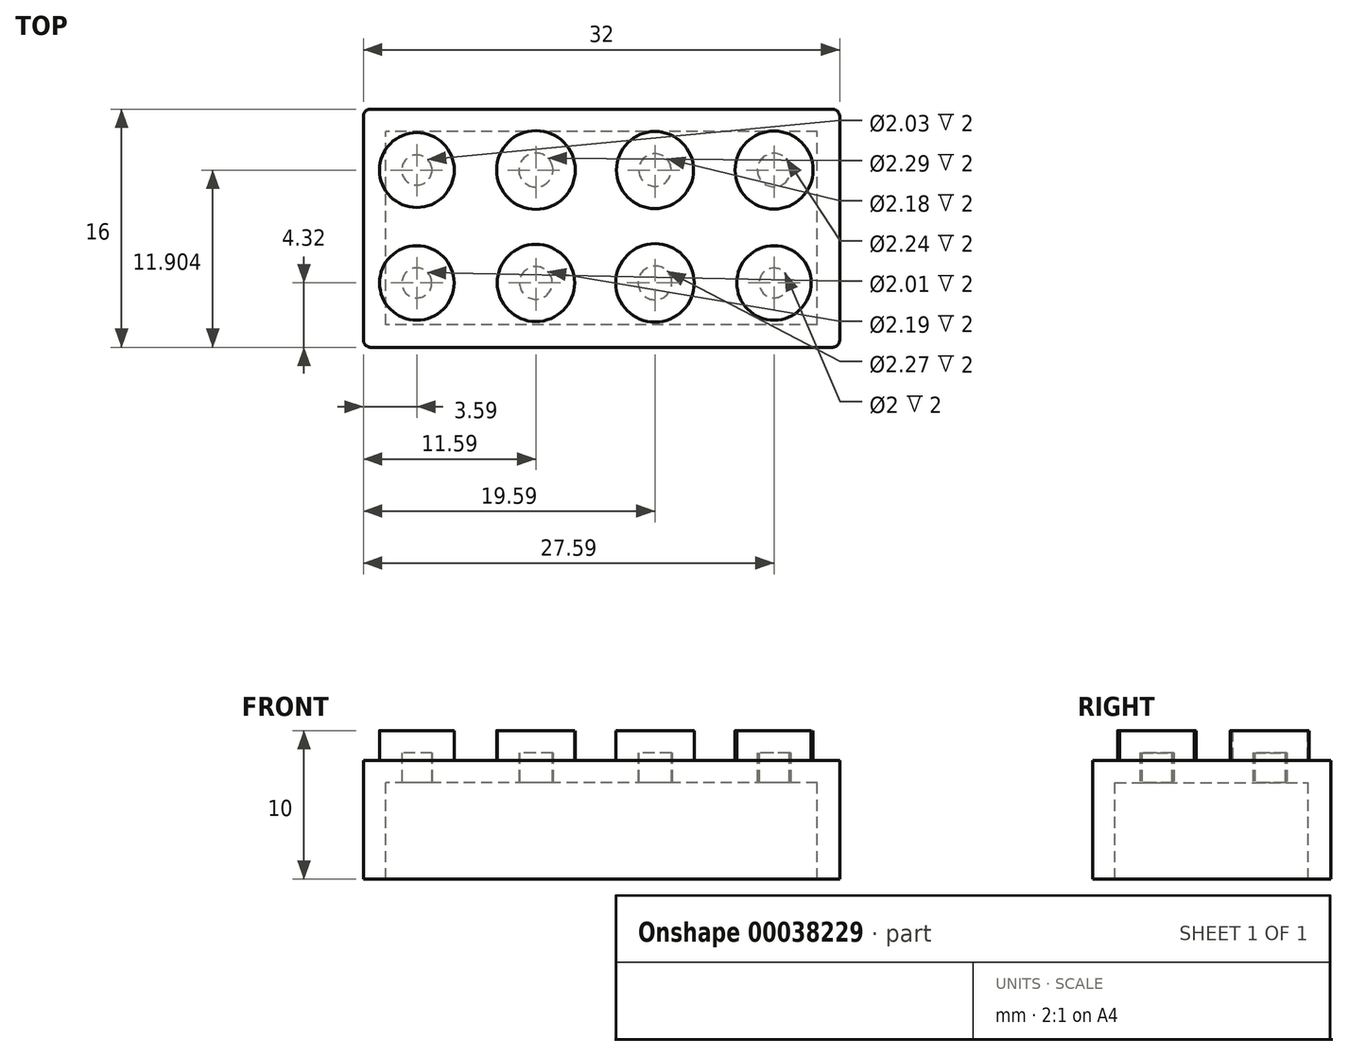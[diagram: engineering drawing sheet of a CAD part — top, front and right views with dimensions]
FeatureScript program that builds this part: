
annotation { "Feature Type Name" : "Feature", "Feature Type Description" : "" }
export const myFeature = defineFeature(function(context is Context, id is Id, definition is map)
    precondition{}
    {
        {
            var Q0;
            Q0=qCreatedBy(makeId("Top.planeOp"),FACE);
            var sketch = newSketch(context, id + "F0", { "sketchPlane" : qUnion([Q0])});
            skLineSegment(sketch, "E0.rect.bottom", {"start": v(16, -6.37) * mm, "end": v(-16, -6.37) * mm});
            skLineSegment(sketch, "E0.rect.top", {"start": v(16, 9.63) * mm, "end": v(-16, 9.63) * mm});
            skLineSegment(sketch, "E0.rect.left", {"start": v(16, -6.37) * mm, "end": v(16, 9.63) * mm});
            skLineSegment(sketch, "E0.rect.right", {"start": v(-16, -6.37) * mm, "end": v(-16, 9.63) * mm});
            skPoint(sketch, "E0.rect.middle", {"position": v(0, 1.63) * mm});
            skSolve(sketch);
        }
        {
            var Q0;
            Q0 = qSketchRegion(id + "F0", true);
            extrude(context, id + "F1", {"entities" : qUnion([Q0]), "depth" : 8 * mm});
        }
        {
            var Q0;
            Q0=qCreatedBy(makeId("Top.planeOp"),FACE);
            var Q1;
            Q1 = qBodyType(qCreatedBy(id + "F3" ,EDGE), BodyType.WIRE);
            cPlane(context, id + "F2", {"entities" : qUnion([Q0, Q1]), "cplaneType" : CPlaneType.OFFSET, "offset" : 8 * mm, "width" : 150 * mm, "height" : 150 * mm});
        }
        {
            var Q0;
            Q0=qCreatedBy(id+"F2.planeOp",FACE);
            var sketch = newSketch(context, id + "F3", { "sketchPlane" : qUnion([Q0])});
            skCircle(sketch, "E1", {"center": v(-12.41, 5.53) * mm, "radius": 2.51 * mm});
            skCircle(sketch, "E2", {"center": v(-4.41, 5.53) * mm, "radius": 2.64 * mm});
            skCircle(sketch, "E3", {"center": v(3.59, 5.53) * mm, "radius": 2.59 * mm});
            skCircle(sketch, "E4", {"center": v(11.59, 5.53) * mm, "radius": 2.62 * mm});
            skCircle(sketch, "E5", {"center": v(-12.41, -2.05) * mm, "radius": 2.5 * mm});
            skCircle(sketch, "E6", {"center": v(-4.41, -2.05) * mm, "radius": 2.6 * mm});
            skCircle(sketch, "E7", {"center": v(3.59, -2.05) * mm, "radius": 2.64 * mm});
            skCircle(sketch, "E8", {"center": v(11.59, -2.05) * mm, "radius": 2.5 * mm});
            skSolve(sketch);
        }
        {
            var Q0;
            Q0=makeQuery(id+"F3.imprint","IMPRINT",FACE,{"disambiguationData":[TD([[makeQuery(id+"F3.imprint","IMPRINT",EDGE,{"derivedFrom":sQuery(id+"F3.wireOp",EDGE,"E3")}),1.0]])]});
            var Q1;
            Q1=makeQuery(id+"F3.imprint","IMPRINT",FACE,{"disambiguationData":[TD([[makeQuery(id+"F3.imprint","IMPRINT",EDGE,{"derivedFrom":sQuery(id+"F3.wireOp",EDGE,"E1")}),1.0]])]});
            var Q2;
            Q2=makeQuery(id+"F3.imprint","IMPRINT",FACE,{"disambiguationData":[TD([[makeQuery(id+"F3.imprint","IMPRINT",EDGE,{"derivedFrom":sQuery(id+"F3.wireOp",EDGE,"E2")}),1.0]])]});
            var Q3;
            Q3=makeQuery(id+"F3.imprint","IMPRINT",FACE,{"disambiguationData":[TD([[makeQuery(id+"F3.imprint","IMPRINT",EDGE,{"derivedFrom":sQuery(id+"F3.wireOp",EDGE,"E5")}),1.0]])]});
            var Q4;
            Q4=makeQuery(id+"F3.imprint","IMPRINT",FACE,{"disambiguationData":[TD([[makeQuery(id+"F3.imprint","IMPRINT",EDGE,{"derivedFrom":sQuery(id+"F3.wireOp",EDGE,"E4")}),1.0]])]});
            var Q5;
            Q5=makeQuery(id+"F3.imprint","IMPRINT",FACE,{"disambiguationData":[TD([[makeQuery(id+"F3.imprint","IMPRINT",EDGE,{"derivedFrom":sQuery(id+"F3.wireOp",EDGE,"E8")}),1.0]])]});
            var Q6;
            Q6=makeQuery(id+"F3.imprint","IMPRINT",FACE,{"disambiguationData":[TD([[makeQuery(id+"F3.imprint","IMPRINT",EDGE,{"derivedFrom":sQuery(id+"F3.wireOp",EDGE,"E7")}),1.0]])]});
            var Q7;
            Q7=makeQuery(id+"F3.imprint","IMPRINT",FACE,{"disambiguationData":[TD([[makeQuery(id+"F3.imprint","IMPRINT",EDGE,{"derivedFrom":sQuery(id+"F3.wireOp",EDGE,"E6")}),1.0]])]});
            extrude(context, id + "F4", {"entities" : qUnion([Q0, Q1, Q2, Q3, Q4, Q5, Q6, Q7]), "operationType" : NewBodyOperationType.ADD, "depth" : 2 * mm});
        }
        {
            var Q0;
            Q0=makeQuery(id+"F1.opExtrude","SWEPT_EDGE",EDGE,{"disambiguationData":[OSD([sQuery(id+"F0.wireOp",EDGE,"E0.rect.top"),sQuery(id+"F0.wireOp",EDGE,"E0.rect.right")])]});
            fillet(context, id + "F5", {"entities" : qUnion([Q0]), "radius" : 0.5 * mm, "tangentPropagation" : true, "allowEdgeOverflow" : false});
        }
        {
            var Q0;
            Q0=makeQuery(id+"F1.opExtrude","SWEPT_EDGE",EDGE,{"disambiguationData":[OSD([sQuery(id+"F0.wireOp",EDGE,"E0.rect.top"),sQuery(id+"F0.wireOp",EDGE,"E0.rect.left")])]});
            fillet(context, id + "F6", {"entities" : qUnion([Q0]), "radius" : 0.5 * mm, "tangentPropagation" : true, "allowEdgeOverflow" : false});
        }
        {
            var Q0;
            Q0=makeQuery(id+"F1.opExtrude","SWEPT_EDGE",EDGE,{"disambiguationData":[OSD([sQuery(id+"F0.wireOp",EDGE,"E0.rect.bottom"),sQuery(id+"F0.wireOp",EDGE,"E0.rect.left")])]});
            var Q1;
            Q1=makeQuery(id+"F1.opExtrude","SWEPT_EDGE",EDGE,{"disambiguationData":[OSD([sQuery(id+"F0.wireOp",EDGE,"E0.rect.bottom"),sQuery(id+"F0.wireOp",EDGE,"E0.rect.right")])]});
            fillet(context, id + "F7", {"entities" : qUnion([Q0, Q1]), "radius" : 0.5 * mm, "tangentPropagation" : true, "allowEdgeOverflow" : false});
        }
        {
            var Q0;
            Q0=makeQuery(id+"F1.opExtrude","CAP_FACE",FACE,{"disambiguationData":[OSD([sQuery(id+"F0.wireOp",EDGE,"E0.rect.bottom"),sQuery(id+"F0.wireOp",EDGE,"E0.rect.top"),sQuery(id+"F0.wireOp",EDGE,"E0.rect.left"),sQuery(id+"F0.wireOp",EDGE,"E0.rect.right")])],"isStart":true});
            shell(context, id + "F8", {"entities" : qUnion([Q0]), "thickness" : 1.5 * mm});
        }
    });
